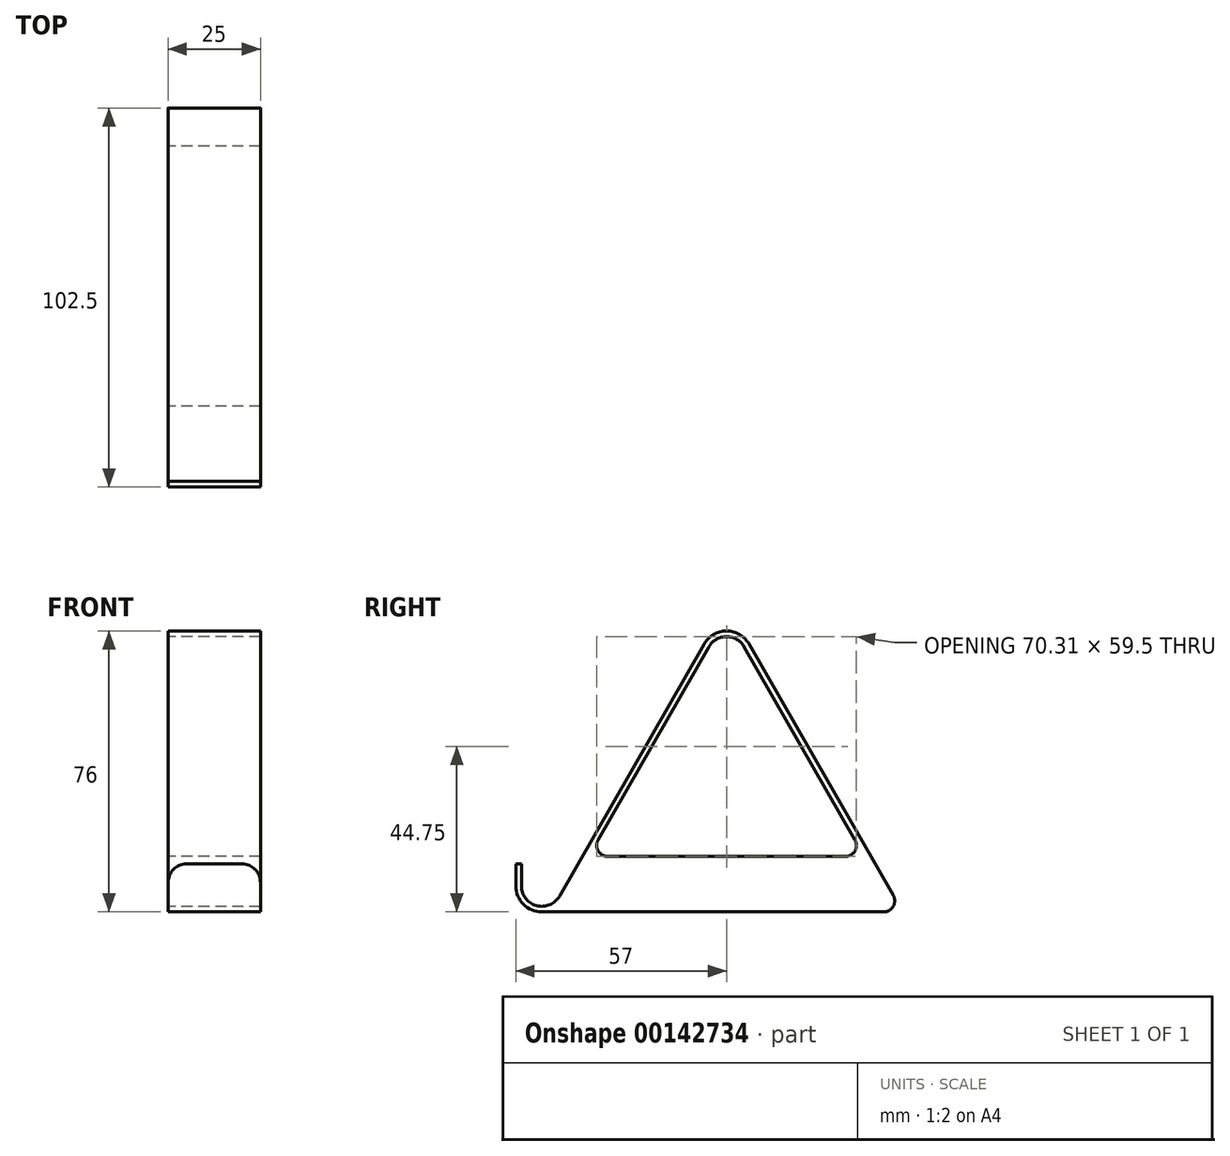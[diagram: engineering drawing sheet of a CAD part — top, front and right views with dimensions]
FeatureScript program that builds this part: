
annotation { "Feature Type Name" : "Feature", "Feature Type Description" : "" }
export const myFeature = defineFeature(function(context is Context, id is Id, definition is map)
    precondition{}
    {
        {
            var Q0;
            Q0=qCreatedBy(makeId("Right.planeOp"),FACE);
            var sketch = newSketch(context, id + "F0", { "sketchPlane" : qUnion([Q0])});
            skArc(sketch, "E0", {"start": v(54.77, 64.74) * mm, "mid": v(50, 67.5) * mm, "end": v(45.23, 64.74) * mm});
            skArc(sketch, "E1", {"start": v(-7, 0) * mm, "mid": v(-4.95, -4.95) * mm, "end": v(0, -7) * mm});
            skLineSegment(sketch, "E2", {"start": v(15.24, 12.5) * mm, "end": v(45.23, 64.74) * mm});
            skLineSegment(sketch, "E3", {"start": v(50, 62) * mm, "end": v(50, -39.77) * mm, "construction": true});
            skLineSegment(sketch, "E4", {"start": v(0, 0) * mm, "end": v(104.66, 0) * mm, "construction": true});
            skLineSegment(sketch, "E5.MirrorCS", {"start": v(84.76, 12.5) * mm, "end": v(54.77, 64.74) * mm});
            skLineSegment(sketch, "E6.MirrorCS", {"start": v(100, 0) * mm, "end": v(-4.66, 0) * mm, "construction": true});
            skLineSegment(sketch, "E7", {"start": v(0, -7) * mm, "end": v(92.5, -7) * mm, "construction": true});
            skLineSegment(sketch, "E8", {"start": v(113.1, -7) * mm, "end": v(113.1, -10.04) * mm, "construction": true});
            skLineSegment(sketch, "E9.1", {"start": v(95.1, -2.5) * mm, "end": v(56.07, 65.48) * mm});
            skArc(sketch, "E9.2", {"start": v(56.07, 65.48) * mm, "mid": v(50, 69) * mm, "end": v(43.93, 65.48) * mm});
            skLineSegment(sketch, "E9.3", {"start": v(4.77, -2.74) * mm, "end": v(43.93, 65.48) * mm});
            skArc(sketch, "E9.4", {"start": v(-5.5, 0.05) * mm, "mid": v(-1.44, -5.3) * mm, "end": v(4.77, -2.74) * mm});
            skLineSegment(sketch, "E10", {"start": v(0, -7) * mm, "end": v(92.5, -7) * mm});
            skLineSegment(sketch, "E11.0", {"start": v(17.84, 8) * mm, "end": v(82.16, 8) * mm});
            skArc(sketch, "E12.filletArc", {"start": v(15.24, 12.5) * mm, "mid": v(15.25, 9.5) * mm, "end": v(17.84, 8) * mm});
            skArc(sketch, "E13.filletArc", {"start": v(82.16, 8) * mm, "mid": v(84.75, 9.5) * mm, "end": v(84.76, 12.5) * mm});
            skArc(sketch, "E14.filletArc", {"start": v(92.5, -7) * mm, "mid": v(95.1, -5.5) * mm, "end": v(95.1, -2.5) * mm});
            skLineSegment(sketch, "E15", {"start": v(-7, 0) * mm, "end": v(-7, 5.98) * mm});
            skLineSegment(sketch, "E16.0", {"start": v(-5.5, 0) * mm, "end": v(-5.5, 5.98) * mm});
            skLineSegment(sketch, "E17", {"start": v(-7, 5.98) * mm, "end": v(-5.5, 5.98) * mm});
            skSolve(sketch);
        }
        {
            var Q0;
            Q0=makeQuery(id+"F0.imprint","IMPRINT",FACE,{"disambiguationData":[TD([[makeQuery(id+"F0.imprint","IMPRINT",EDGE,{"derivedFrom":sQuery(id+"F0.wireOp",EDGE,"E0")}),-1.0]])]});
            extrude(context, id + "F1", {"entities" : qUnion([Q0]), "depth" : 25 * mm});
        }
        {
            var Q0;
            Q0=makeQuery(id+"F1.opExtrude","CAP_EDGE",EDGE,{"disambiguationData":[OSD([sQuery(id+"F0.wireOp",EDGE,"E17")])],"isStart":true});
            var Q1;
            Q1=makeQuery(id+"F1.opExtrude","CAP_EDGE",EDGE,{"disambiguationData":[OSD([sQuery(id+"F0.wireOp",EDGE,"E17")])],"isStart":false});
            fillet(context, id + "F2", {"entities" : qUnion([Q0, Q1]), "radius" : 5 * mm, "tangentPropagation" : true, "allowEdgeOverflow" : false});
        }
    });
